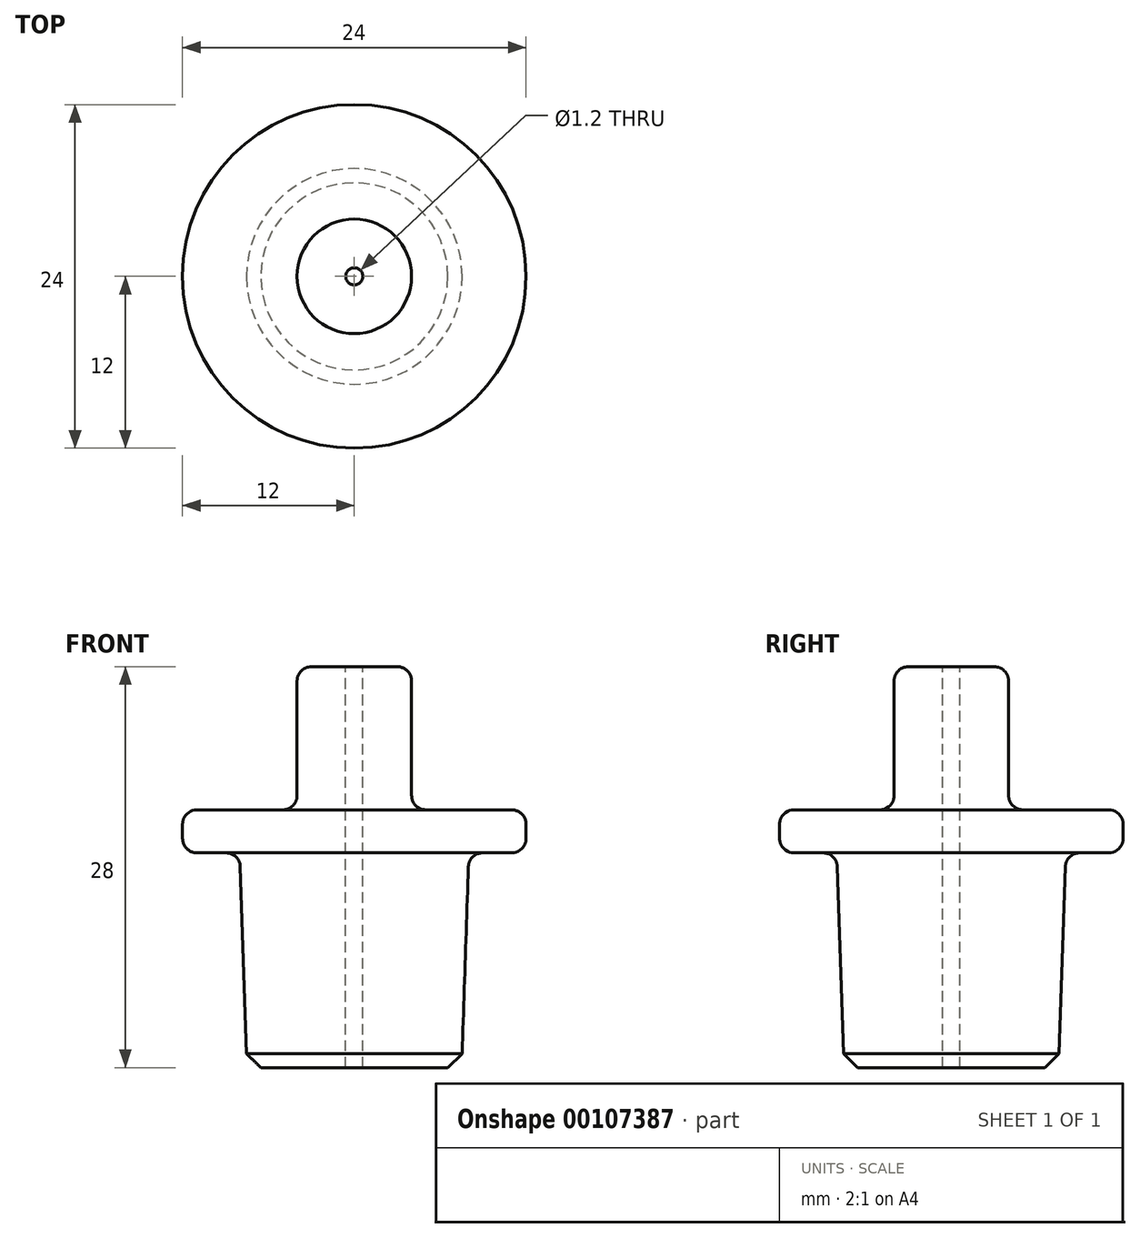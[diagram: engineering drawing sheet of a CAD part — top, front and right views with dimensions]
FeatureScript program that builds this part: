
annotation { "Feature Type Name" : "Feature", "Feature Type Description" : "" }
export const myFeature = defineFeature(function(context is Context, id is Id, definition is map)
    precondition{}
    {
        {
            var Q0;
            Q0=qCreatedBy(makeId("Front.planeOp"),FACE);
            var sketch = newSketch(context, id + "F0", { "sketchPlane" : qUnion([Q0])});
            skLineSegment(sketch, "E0", {"start": v(0, 10.35) * mm, "end": v(0, -9.76) * mm, "construction": true});
            skLineSegment(sketch, "E1", {"start": v(0.6, 16.68) * mm, "end": v(0.6, -11.32) * mm});
            skLineSegment(sketch, "E2", {"start": v(0.6, 16.68) * mm, "end": v(4, 16.68) * mm});
            skLineSegment(sketch, "E3", {"start": v(4, 16.68) * mm, "end": v(4, 6.68) * mm});
            skLineSegment(sketch, "E4", {"start": v(4, 6.68) * mm, "end": v(12, 6.68) * mm});
            skLineSegment(sketch, "E5", {"start": v(12, 6.68) * mm, "end": v(12, 3.68) * mm});
            skLineSegment(sketch, "E6", {"start": v(12, 3.68) * mm, "end": v(8, 3.68) * mm});
            skLineSegment(sketch, "E7", {"start": v(8, 3.68) * mm, "end": v(7.5, -11.32) * mm});
            skLineSegment(sketch, "E8", {"start": v(7.5, -11.32) * mm, "end": v(0.6, -11.32) * mm});
            skSolve(sketch);
        }
        {
            var Q0;
            Q0=makeQuery(id+"F0.imprint","IMPRINT",FACE,{"disambiguationData":[TD([[makeQuery(id+"F0.imprint","IMPRINT",EDGE,{"derivedFrom":sQuery(id+"F0.wireOp",EDGE,"E1")}),1.0]])]});
            var Q1;
            Q1=makeQuery(id+"F0.imprint","IMPRINT",FACE,{"disambiguationData":[TD([[makeQuery(id+"F0.imprint","IMPRINT",EDGE,{"derivedFrom":sQuery(id+"F0.wireOp",EDGE,"E1")}),1.0]])]});
            var Q2;
            Q2=sQuery(id+"F0.wireOp",EDGE,"E0");
            revolve(context, id + "F1", {"entities" : qUnion([Q0, Q1]), "axis" : qUnion([Q2]), "revolveType" : RevolveType.FULL});
        }
        {
            var Q0;
            Q0=makeQuery(id+"F1.opRevolve","SWEPT_EDGE",EDGE,{"disambiguationData":[OSD([sQuery(id+"F0.wireOp",EDGE,"E6"),sQuery(id+"F0.wireOp",EDGE,"E7")])]});
            var Q1;
            Q1=makeQuery(id+"F1.opRevolve","SWEPT_EDGE",EDGE,{"disambiguationData":[OSD([sQuery(id+"F0.wireOp",EDGE,"E5"),sQuery(id+"F0.wireOp",EDGE,"E6")])]});
            var Q2;
            Q2=makeQuery(id+"F1.opRevolve","SWEPT_EDGE",EDGE,{"disambiguationData":[OSD([sQuery(id+"F0.wireOp",EDGE,"E4"),sQuery(id+"F0.wireOp",EDGE,"E5")])]});
            var Q3;
            Q3=makeQuery(id+"F1.opRevolve","SWEPT_EDGE",EDGE,{"disambiguationData":[OSD([sQuery(id+"F0.wireOp",EDGE,"E2"),sQuery(id+"F0.wireOp",EDGE,"E3")])]});
            var Q4;
            Q4=makeQuery(id+"F1.opRevolve","SWEPT_EDGE",EDGE,{"disambiguationData":[OSD([sQuery(id+"F0.wireOp",EDGE,"E3"),sQuery(id+"F0.wireOp",EDGE,"E4")])]});
            fillet(context, id + "F2", {"entities" : qUnion([Q0, Q1, Q2, Q3, Q4]), "radius" : 1 * mm, "tangentPropagation" : true, "allowEdgeOverflow" : false});
        }
        {
            var Q0;
            Q0=makeQuery(id+"F1.opRevolve","SWEPT_EDGE",EDGE,{"disambiguationData":[OSD([sQuery(id+"F0.wireOp",EDGE,"E7"),sQuery(id+"F0.wireOp",EDGE,"E8")])]});
            chamfer(context, id + "F3", {"entities" : qUnion([Q0]), "width" : 1 * mm, "tangentPropagation" : true});
        }
    });
